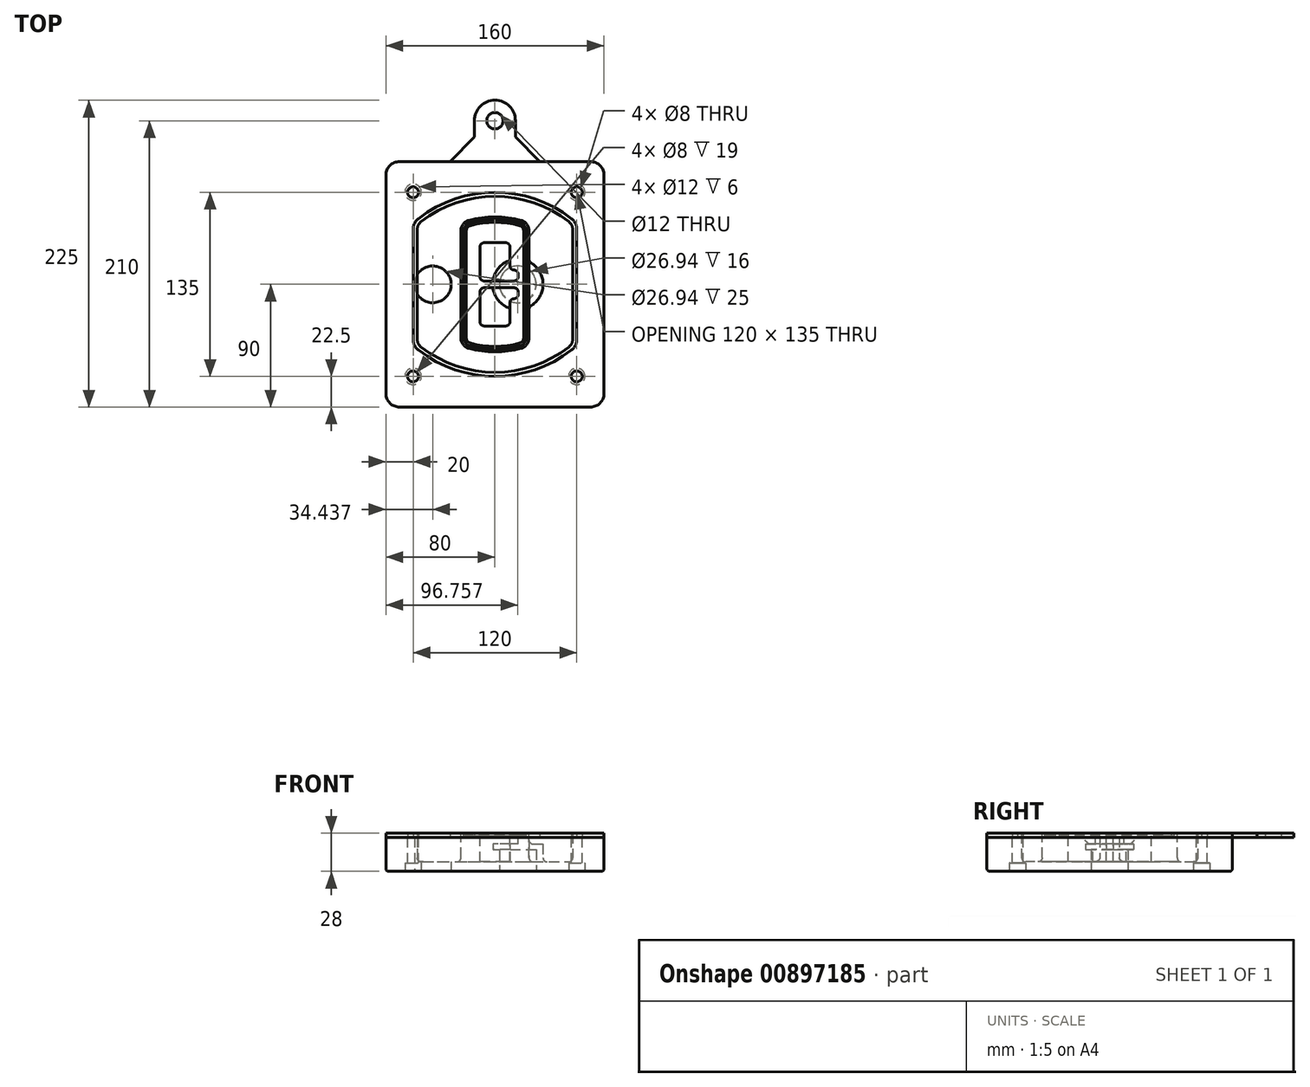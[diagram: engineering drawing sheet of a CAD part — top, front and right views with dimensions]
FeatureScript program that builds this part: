
annotation { "Feature Type Name" : "Feature", "Feature Type Description" : "" }
export const myFeature = defineFeature(function(context is Context, id is Id, definition is map)
    precondition{}
    {
        {
            var Q0;
            Q0=qCreatedBy(makeId("Top.planeOp"),FACE);
            var sketch = newSketch(context, id + "F0", { "sketchPlane" : qUnion([Q0])});
            skPoint(sketch, "E0.rect.middle", {"position": v(0, 0) * mm});
            skLineSegment(sketch, "E1.bottom", {"start": v(-70, -90) * mm, "end": v(70, -90) * mm});
            skLineSegment(sketch, "E1.top", {"start": v(-70, 90) * mm, "end": v(70, 90) * mm});
            skLineSegment(sketch, "E1.left", {"start": v(-80, -80) * mm, "end": v(-80, 80) * mm});
            skLineSegment(sketch, "E1.right", {"start": v(80, -80) * mm, "end": v(80, 80) * mm});
            skLineSegment(sketch, "E2", {"start": v(-80, 90) * mm, "end": v(80, -90) * mm, "construction": true});
            skLineSegment(sketch, "E3", {"start": v(80, 90) * mm, "end": v(-80, -90) * mm, "construction": true});
            skCircle(sketch, "E4", {"center": v(-60, 67.5) * mm, "radius": 4 * mm});
            skCircle(sketch, "E5", {"center": v(60, 67.5) * mm, "radius": 4 * mm});
            skCircle(sketch, "E6", {"center": v(60, -67.5) * mm, "radius": 4 * mm});
            skCircle(sketch, "E7", {"center": v(-60, -67.5) * mm, "radius": 4 * mm});
            skLineSegment(sketch, "E8", {"start": v(-60, 67.5) * mm, "end": v(60, 67.5) * mm, "construction": true});
            skLineSegment(sketch, "E9", {"start": v(60, 67.5) * mm, "end": v(60, -67.5) * mm, "construction": true});
            skLineSegment(sketch, "E10", {"start": v(60, -67.5) * mm, "end": v(-60, -67.5) * mm, "construction": true});
            skLineSegment(sketch, "E11", {"start": v(-60, -67.5) * mm, "end": v(-60, 67.5) * mm, "construction": true});
            skLineSegment(sketch, "E12", {"start": v(-60, 40.3) * mm, "end": v(-60, -40.3) * mm});
            skLineSegment(sketch, "E13", {"start": v(60, 40.3) * mm, "end": v(60, -40.3) * mm});
            skArc(sketch, "E14", {"start": v(56.15, 48.18) * mm, "mid": v(0, 67.5) * mm, "end": v(-56.15, 48.18) * mm});
            skArc(sketch, "E15", {"start": v(-56.15, -48.18) * mm, "mid": v(0, -67.5) * mm, "end": v(56.15, -48.18) * mm});
            skLineSegment(sketch, "E16", {"start": v(-60, 0) * mm, "end": v(60, 0) * mm, "construction": true});
            skPoint(sketch, "E17.visualSharp", {"position": v(-60, -45) * mm});
            skArc(sketch, "E17.filletArc", {"start": v(-60, -40.3) * mm, "mid": v(-58.99, -44.68) * mm, "end": v(-56.15, -48.18) * mm});
            skPoint(sketch, "E18.visualSharp", {"position": v(-60, 45) * mm});
            skArc(sketch, "E18.filletArc", {"start": v(-56.15, 48.18) * mm, "mid": v(-58.99, 44.68) * mm, "end": v(-60, 40.3) * mm});
            skPoint(sketch, "E19.visualSharp", {"position": v(60, 45) * mm});
            skArc(sketch, "E19.filletArc", {"start": v(60, 40.3) * mm, "mid": v(58.99, 44.68) * mm, "end": v(56.15, 48.18) * mm});
            skPoint(sketch, "E20.visualSharp", {"position": v(60, -45) * mm});
            skArc(sketch, "E20.filletArc", {"start": v(56.15, -48.18) * mm, "mid": v(58.99, -44.68) * mm, "end": v(60, -40.3) * mm});
            skPoint(sketch, "E21.visualSharp", {"position": v(-80, 90) * mm});
            skArc(sketch, "E21.filletArc", {"start": v(-70, 90) * mm, "mid": v(-77.07, 87.07) * mm, "end": v(-80, 80) * mm});
            skPoint(sketch, "E22.visualSharp", {"position": v(80, 90) * mm});
            skArc(sketch, "E22.filletArc", {"start": v(80, 80) * mm, "mid": v(77.07, 87.07) * mm, "end": v(70, 90) * mm});
            skPoint(sketch, "E23.visualSharp", {"position": v(80, -90) * mm});
            skArc(sketch, "E23.filletArc", {"start": v(70, -90) * mm, "mid": v(77.07, -87.07) * mm, "end": v(80, -80) * mm});
            skPoint(sketch, "E24.visualSharp", {"position": v(-80, -90) * mm});
            skArc(sketch, "E24.filletArc", {"start": v(-80, -80) * mm, "mid": v(-77.07, -87.07) * mm, "end": v(-70, -90) * mm});
            skArc(sketch, "E25.0", {"start": v(57, 40.3) * mm, "mid": v(56.3, 43.36) * mm, "end": v(54.3, 45.81) * mm});
            skLineSegment(sketch, "E25.1", {"start": v(57, 40.3) * mm, "end": v(57, -40.3) * mm});
            skArc(sketch, "E25.2", {"start": v(54.3, -45.81) * mm, "mid": v(56.3, -43.36) * mm, "end": v(57, -40.3) * mm});
            skArc(sketch, "E25.3", {"start": v(-54.3, -45.81) * mm, "mid": v(0, -64.5) * mm, "end": v(54.3, -45.81) * mm});
            skArc(sketch, "E25.4", {"start": v(-57, -40.3) * mm, "mid": v(-56.3, -43.36) * mm, "end": v(-54.3, -45.81) * mm});
            skArc(sketch, "E25.5", {"start": v(54.3, 45.81) * mm, "mid": v(0, 64.5) * mm, "end": v(-54.3, 45.81) * mm});
            skLineSegment(sketch, "E25.6", {"start": v(-57, 40.3) * mm, "end": v(-57, -40.3) * mm});
            skArc(sketch, "E25.7", {"start": v(-54.3, 45.81) * mm, "mid": v(-56.3, 43.36) * mm, "end": v(-57, 40.3) * mm});
            skArc(sketch, "E26.0", {"start": v(-58.62, 51.33) * mm, "mid": v(-62.58, 46.43) * mm, "end": v(-64, 40.3) * mm});
            skArc(sketch, "E26.1", {"start": v(58.62, 51.33) * mm, "mid": v(0, 71.5) * mm, "end": v(-58.62, 51.33) * mm});
            skArc(sketch, "E26.2", {"start": v(64, 40.3) * mm, "mid": v(62.58, 46.43) * mm, "end": v(58.62, 51.33) * mm});
            skLineSegment(sketch, "E26.3", {"start": v(64, 40.3) * mm, "end": v(64, -40.3) * mm});
            skArc(sketch, "E26.4", {"start": v(58.62, -51.33) * mm, "mid": v(62.58, -46.43) * mm, "end": v(64, -40.3) * mm});
            skLineSegment(sketch, "E26.5", {"start": v(-64, 40.3) * mm, "end": v(-64, -40.3) * mm});
            skArc(sketch, "E26.6", {"start": v(-58.62, -51.33) * mm, "mid": v(0, -71.5) * mm, "end": v(58.62, -51.33) * mm});
            skArc(sketch, "E26.7", {"start": v(-64, -40.3) * mm, "mid": v(-62.58, -46.43) * mm, "end": v(-58.62, -51.33) * mm});
            skSolve(sketch);
        }
        {
            var Q0;
            Q0=makeQuery(id+"F0.imprint","IMPRINT",FACE,{"disambiguationData":[TD([[makeQuery(id+"F0.imprint","IMPRINT",EDGE,{"derivedFrom":sQuery(id+"F0.wireOp",EDGE,"E1.bottom")}),1.0]])]});
            var Q1;
            Q1=makeQuery(id+"F0.imprint","IMPRINT",FACE,{"disambiguationData":[TD([[makeQuery(id+"F0.imprint","IMPRINT",EDGE,{"derivedFrom":sQuery(id+"F0.wireOp",EDGE,"E12")}),1.0]])]});
            var Q2;
            Q2=makeQuery(id+"F0.imprint","IMPRINT",FACE,{"disambiguationData":[TD([[makeQuery(id+"F0.imprint","IMPRINT",EDGE,{"derivedFrom":sQuery(id+"F0.wireOp",EDGE,"E25.0")}),1.0]])]});
            var Q3;
            Q3=makeQuery(id+"F0.imprint","IMPRINT",FACE,{"disambiguationData":[TD([[makeQuery(id+"F0.imprint","IMPRINT",EDGE,{"derivedFrom":sQuery(id+"F0.wireOp",EDGE,"E12")}),-1.0]])]});
            extrude(context, id + "F1", {"entities" : qUnion([Q0, Q1, Q2, Q3]), "oppositeDirection" : true, "depth" : 25 * mm});
        }
        {
            var Q0;
            Q0=makeQuery(id+"F0.imprint","IMPRINT",FACE,{"disambiguationData":[TD([[makeQuery(id+"F0.imprint","IMPRINT",EDGE,{"derivedFrom":sQuery(id+"F0.wireOp",EDGE,"E12")}),1.0]])]});
            extrude(context, id + "F2", {"entities" : qUnion([Q0]), "operationType" : NewBodyOperationType.ADD, "depth" : 3 * mm});
        }
        {
            var Q0;
            Q0=makeQuery(id+"F0.imprint","IMPRINT",FACE,{"disambiguationData":[TD([[makeQuery(id+"F0.imprint","IMPRINT",EDGE,{"derivedFrom":sQuery(id+"F0.wireOp",EDGE,"E25.0")}),1.0]])]});
            extrude(context, id + "F3", {"entities" : qUnion([Q0]), "operationType" : NewBodyOperationType.REMOVE, "oppositeDirection" : true, "depth" : 18 * mm});
        }
        {
            var Q0;
            Q0=makeQuery(id+"F2.opExtrude","CAP_FACE",FACE,{"disambiguationData":[OSD([sQuery(id+"F0.wireOp",EDGE,"E12"),sQuery(id+"F0.wireOp",EDGE,"E13"),sQuery(id+"F0.wireOp",EDGE,"E14"),sQuery(id+"F0.wireOp",EDGE,"E15"),sQuery(id+"F0.wireOp",EDGE,"E17.filletArc"),sQuery(id+"F0.wireOp",EDGE,"E18.filletArc"),sQuery(id+"F0.wireOp",EDGE,"E19.filletArc"),sQuery(id+"F0.wireOp",EDGE,"E20.filletArc"),sQuery(id+"F0.wireOp",EDGE,"E25.0"),sQuery(id+"F0.wireOp",EDGE,"E25.1"),sQuery(id+"F0.wireOp",EDGE,"E25.2"),sQuery(id+"F0.wireOp",EDGE,"E25.3"),sQuery(id+"F0.wireOp",EDGE,"E25.4"),sQuery(id+"F0.wireOp",EDGE,"E25.5"),sQuery(id+"F0.wireOp",EDGE,"E25.6"),sQuery(id+"F0.wireOp",EDGE,"E25.7")])],"isStart":false});
            var sketch = newSketch(context, id + "F4", { "sketchPlane" : qUnion([Q0])});
            skArc(sketch, "E27.0", {"start": v(-19.08, -46.97) * mm, "mid": v(0, -49.5) * mm, "end": v(19.08, -46.97) * mm});
            skArc(sketch, "E28.0", {"start": v(19.08, 46.97) * mm, "mid": v(0, 49.5) * mm, "end": v(-19.08, 46.97) * mm});
            skLineSegment(sketch, "E29", {"start": v(-25, 39.25) * mm, "end": v(-25, -39.25) * mm});
            skLineSegment(sketch, "E30", {"start": v(25, 39.25) * mm, "end": v(25, -39.25) * mm});
            skLineSegment(sketch, "E31", {"start": v(-25, 45.1) * mm, "end": v(25, 45.1) * mm, "construction": true});
            skLineSegment(sketch, "E32", {"start": v(-25, -45.1) * mm, "end": v(25, -45.1) * mm, "construction": true});
            skPoint(sketch, "E33.visualSharp", {"position": v(-25, 45.1) * mm});
            skArc(sketch, "E33.filletArc", {"start": v(-19.08, 46.97) * mm, "mid": v(-23.35, 44.11) * mm, "end": v(-25, 39.25) * mm});
            skPoint(sketch, "E34.visualSharp", {"position": v(25, 45.1) * mm});
            skArc(sketch, "E34.filletArc", {"start": v(25, 39.25) * mm, "mid": v(23.35, 44.11) * mm, "end": v(19.08, 46.97) * mm});
            skPoint(sketch, "E35.visualSharp", {"position": v(25, -45.1) * mm});
            skArc(sketch, "E35.filletArc", {"start": v(19.08, -46.97) * mm, "mid": v(23.35, -44.11) * mm, "end": v(25, -39.25) * mm});
            skPoint(sketch, "E36.visualSharp", {"position": v(-25, -45.1) * mm});
            skArc(sketch, "E36.filletArc", {"start": v(-25, -39.25) * mm, "mid": v(-23.35, -44.11) * mm, "end": v(-19.08, -46.97) * mm});
            skArc(sketch, "E37.0", {"start": v(54.3, 45.81) * mm, "mid": v(0, 64.5) * mm, "end": v(-54.3, 45.81) * mm});
            skArc(sketch, "E37.1", {"start": v(-54.3, 45.81) * mm, "mid": v(-56.3, 43.36) * mm, "end": v(-57, 40.3) * mm});
            skLineSegment(sketch, "E37.2", {"start": v(-57, 40.3) * mm, "end": v(-57, -40.3) * mm});
            skArc(sketch, "E37.3", {"start": v(-57, -40.3) * mm, "mid": v(-56.3, -43.36) * mm, "end": v(-54.3, -45.81) * mm});
            skArc(sketch, "E37.4", {"start": v(-54.3, -45.81) * mm, "mid": v(0, -64.5) * mm, "end": v(54.3, -45.81) * mm});
            skArc(sketch, "E37.5", {"start": v(54.3, -45.81) * mm, "mid": v(56.3, -43.36) * mm, "end": v(57, -40.3) * mm});
            skLineSegment(sketch, "E37.6", {"start": v(57, 40.3) * mm, "end": v(57, -40.3) * mm});
            skArc(sketch, "E37.7", {"start": v(57, 40.3) * mm, "mid": v(56.3, 43.36) * mm, "end": v(54.3, 45.81) * mm});
            skLineSegment(sketch, "E38.0", {"start": v(23, 39.25) * mm, "end": v(23, -39.25) * mm});
            skArc(sketch, "E38.1", {"start": v(18.56, -45.04) * mm, "mid": v(21.76, -42.9) * mm, "end": v(23, -39.25) * mm});
            skArc(sketch, "E38.2", {"start": v(-18.56, -45.04) * mm, "mid": v(0, -47.5) * mm, "end": v(18.56, -45.04) * mm});
            skArc(sketch, "E38.3", {"start": v(-23, -39.25) * mm, "mid": v(-21.76, -42.9) * mm, "end": v(-18.56, -45.04) * mm});
            skLineSegment(sketch, "E38.4", {"start": v(-23, 39.25) * mm, "end": v(-23, -39.25) * mm});
            skArc(sketch, "E38.5", {"start": v(23, 39.25) * mm, "mid": v(21.76, 42.9) * mm, "end": v(18.56, 45.04) * mm});
            skArc(sketch, "E38.6", {"start": v(-18.56, 45.04) * mm, "mid": v(-21.76, 42.9) * mm, "end": v(-23, 39.25) * mm});
            skArc(sketch, "E38.7", {"start": v(18.56, 45.04) * mm, "mid": v(0, 47.5) * mm, "end": v(-18.56, 45.04) * mm});
            skArc(sketch, "E39.0", {"start": v(21, 39.25) * mm, "mid": v(20.18, 41.68) * mm, "end": v(18.04, 43.1) * mm});
            skLineSegment(sketch, "E39.1", {"start": v(21, 39.25) * mm, "end": v(21, -39.25) * mm});
            skArc(sketch, "E39.2", {"start": v(18.04, -43.1) * mm, "mid": v(20.18, -41.68) * mm, "end": v(21, -39.25) * mm});
            skArc(sketch, "E39.3", {"start": v(-18.04, -43.1) * mm, "mid": v(0, -45.5) * mm, "end": v(18.04, -43.1) * mm});
            skArc(sketch, "E39.4", {"start": v(-21, -39.25) * mm, "mid": v(-20.18, -41.68) * mm, "end": v(-18.04, -43.1) * mm});
            skArc(sketch, "E39.5", {"start": v(18.04, 43.1) * mm, "mid": v(0, 45.5) * mm, "end": v(-18.04, 43.1) * mm});
            skLineSegment(sketch, "E39.6", {"start": v(-21, 39.25) * mm, "end": v(-21, -39.25) * mm});
            skArc(sketch, "E39.7", {"start": v(-18.04, 43.1) * mm, "mid": v(-20.18, 41.68) * mm, "end": v(-21, 39.25) * mm});
            skLineSegment(sketch, "E40", {"start": v(-25, 0) * mm, "end": v(25, 0) * mm, "construction": true});
            skLineSegment(sketch, "E41", {"start": v(-11, 5.5) * mm, "end": v(-11, 27.5) * mm});
            skLineSegment(sketch, "E42", {"start": v(-8, 30.5) * mm, "end": v(8, 30.5) * mm});
            skLineSegment(sketch, "E43", {"start": v(11, 27.5) * mm, "end": v(11, 13.5) * mm});
            skLineSegment(sketch, "E44", {"start": v(14, 10.5) * mm, "end": v(14, 10.5) * mm});
            skLineSegment(sketch, "E45", {"start": v(17, 7.5) * mm, "end": v(17, 5.5) * mm});
            skLineSegment(sketch, "E46", {"start": v(14, 2.5) * mm, "end": v(-8, 2.5) * mm});
            skPoint(sketch, "E47.visualSharp", {"position": v(-11, 30.5) * mm});
            skArc(sketch, "E47.filletArc", {"start": v(-8, 30.5) * mm, "mid": v(-10.12, 29.62) * mm, "end": v(-11, 27.5) * mm});
            skPoint(sketch, "E48.visualSharp", {"position": v(11, 30.5) * mm});
            skArc(sketch, "E48.filletArc", {"start": v(11, 27.5) * mm, "mid": v(10.12, 29.62) * mm, "end": v(8, 30.5) * mm});
            skPoint(sketch, "E49.visualSharp", {"position": v(11, 10.5) * mm});
            skArc(sketch, "E49.filletArc", {"start": v(11, 13.5) * mm, "mid": v(11.88, 11.38) * mm, "end": v(14, 10.5) * mm});
            skPoint(sketch, "E50.visualSharp", {"position": v(17, 10.5) * mm});
            skArc(sketch, "E50.filletArc", {"start": v(17, 7.5) * mm, "mid": v(16.12, 9.62) * mm, "end": v(14, 10.5) * mm});
            skPoint(sketch, "E51.visualSharp", {"position": v(17, 2.5) * mm});
            skArc(sketch, "E51.filletArc", {"start": v(14, 2.5) * mm, "mid": v(16.12, 3.38) * mm, "end": v(17, 5.5) * mm});
            skPoint(sketch, "E52.visualSharp", {"position": v(-11, 2.5) * mm});
            skArc(sketch, "E52.filletArc", {"start": v(-11, 5.5) * mm, "mid": v(-10.12, 3.38) * mm, "end": v(-8, 2.5) * mm});
            skLineSegment(sketch, "E53.0.MirrorCS", {"start": v(14, -2.5) * mm, "end": v(-8, -2.5) * mm});
            skArc(sketch, "E54.0.MirrorCS", {"start": v(-11, -5.5) * mm, "mid": v(-10.12, -3.38) * mm, "end": v(-8, -2.5) * mm});
            skLineSegment(sketch, "E55.0.MirrorCS", {"start": v(-11, -5.5) * mm, "end": v(-11, -27.5) * mm});
            skArc(sketch, "E56.0.MirrorCS", {"start": v(-8, -30.5) * mm, "mid": v(-10.12, -29.62) * mm, "end": v(-11, -27.5) * mm});
            skLineSegment(sketch, "E57.0.MirrorCS", {"start": v(-8, -30.5) * mm, "end": v(8, -30.5) * mm});
            skArc(sketch, "E58.0.MirrorCS", {"start": v(11, -27.5) * mm, "mid": v(10.12, -29.62) * mm, "end": v(8, -30.5) * mm});
            skLineSegment(sketch, "E59.0.MirrorCS", {"start": v(11, -27.5) * mm, "end": v(11, -13.5) * mm});
            skArc(sketch, "E60.0.MirrorCS", {"start": v(11, -13.5) * mm, "mid": v(11.88, -11.38) * mm, "end": v(14, -10.5) * mm});
            skArc(sketch, "E61.0.MirrorCS", {"start": v(17, -7.5) * mm, "mid": v(16.12, -9.62) * mm, "end": v(14, -10.5) * mm});
            skLineSegment(sketch, "E62.0.MirrorCS", {"start": v(17, -7.5) * mm, "end": v(17, -5.5) * mm});
            skArc(sketch, "E63.0.MirrorCS", {"start": v(14, -2.5) * mm, "mid": v(16.12, -3.38) * mm, "end": v(17, -5.5) * mm});
            skSolve(sketch);
        }
        {
            var Q0;
            Q0=makeQuery(id+"F4.imprint","IMPRINT",FACE,{"disambiguationData":[TD([[makeQuery(id+"F4.imprint","IMPRINT",EDGE,{"derivedFrom":sQuery(id+"F4.wireOp",EDGE,"E27.0")}),1.0]])]});
            var Q1;
            Q1=makeQuery(id+"F4.imprint","IMPRINT",FACE,{"disambiguationData":[TD([[makeQuery(id+"F4.imprint","IMPRINT",EDGE,{"derivedFrom":sQuery(id+"F4.wireOp",EDGE,"E38.0")}),-1.0]])]});
            var Q2;
            Q2=makeQuery(id+"F4.imprint","IMPRINT",FACE,{"disambiguationData":[TD([[makeQuery(id+"F4.imprint","IMPRINT",EDGE,{"derivedFrom":sQuery(id+"F4.wireOp",EDGE,"E39.0")}),1.0]])]});
            extrude(context, id + "F5", {"entities" : qUnion([Q0, Q1, Q2]), "operationType" : NewBodyOperationType.ADD, "endBound" : BoundingType.UP_TO_NEXT, "oppositeDirection" : true, "depth" : 25 * mm});
        }
        {
            var Q0;
            Q0=makeQuery(id+"F4.imprint","IMPRINT",FACE,{"disambiguationData":[TD([[makeQuery(id+"F4.imprint","IMPRINT",EDGE,{"derivedFrom":sQuery(id+"F4.wireOp",EDGE,"E38.0")}),-1.0]])]});
            extrude(context, id + "F6", {"entities" : qUnion([Q0]), "operationType" : NewBodyOperationType.REMOVE, "oppositeDirection" : true, "depth" : 2 * mm});
        }
        {
            var Q0;
            Q0=makeQuery(id+"F1.opExtrude","CAP_FACE",FACE,{"disambiguationData":[OSD([sQuery(id+"F0.wireOp",EDGE,"E1.bottom"),sQuery(id+"F0.wireOp",EDGE,"E1.top"),sQuery(id+"F0.wireOp",EDGE,"E1.left"),sQuery(id+"F0.wireOp",EDGE,"E1.right"),sQuery(id+"F0.wireOp",EDGE,"E4"),sQuery(id+"F0.wireOp",EDGE,"E5"),sQuery(id+"F0.wireOp",EDGE,"E6"),sQuery(id+"F0.wireOp",EDGE,"E7"),sQuery(id+"F0.wireOp",EDGE,"E21.filletArc"),sQuery(id+"F0.wireOp",EDGE,"E22.filletArc"),sQuery(id+"F0.wireOp",EDGE,"E23.filletArc"),sQuery(id+"F0.wireOp",EDGE,"E24.filletArc")])],"isStart":false});
            var sketch = newSketch(context, id + "F7", { "sketchPlane" : qUnion([Q0])});
            skCircle(sketch, "E64", {"center": v(16.76, 0) * mm, "radius": 13.47 * mm});
            skCircle(sketch, "E65", {"center": v(-45.56, 0) * mm, "radius": 13.47 * mm});
            skLineSegment(sketch, "E66", {"start": v(80, 0) * mm, "end": v(-80, 0) * mm});
            skCircle(sketch, "E67", {"center": v(16.76, 0) * mm, "radius": 18.47 * mm});
            skCircle(sketch, "E68", {"center": v(60, -67.5) * mm, "radius": 6 * mm});
            skCircle(sketch, "E69", {"center": v(-60, -67.5) * mm, "radius": 6 * mm});
            skCircle(sketch, "E70", {"center": v(-60, 67.5) * mm, "radius": 6 * mm});
            skCircle(sketch, "E71", {"center": v(60, 67.5) * mm, "radius": 6 * mm});
            skSolve(sketch);
        }
        {
            var Q0;
            {var subQ1=sQuery(id+"F7.wireOp",EDGE,"E66");var subQ4=sQuery(id+"F7.wireOp",EDGE,"E64");var subQ6=makeQuery(id+"F7.imprint","INTERSECT",VERTEX,{"disambiguationData":[OD(0.0)],"derivedFrom":[subQ4,subQ1]});Q0=makeQuery(id+"F7.imprint","IMPRINT",FACE,{"disambiguationData":[TD([[makeQuery(id+"F7.imprint","IMPRINT",EDGE,{"disambiguationData":[TD([[subQ6,-1.0]])],"derivedFrom":subQ4}),-1.0]])]});}
            var Q1;
            {var subQ0=sQuery(id+"F7.wireOp",EDGE,"E66");var subQ1=sQuery(id+"F7.wireOp",EDGE,"E64");var subQ3=makeQuery(id+"F7.imprint","INTERSECT",VERTEX,{"disambiguationData":[OD(0.0)],"derivedFrom":[subQ1,subQ0]});Q1=makeQuery(id+"F7.imprint","IMPRINT",FACE,{"disambiguationData":[TD([[makeQuery(id+"F7.imprint","IMPRINT",EDGE,{"disambiguationData":[TD([[subQ3,-1.0]])],"derivedFrom":subQ1}),1.0]])]});}
            var Q2;
            {var subQ0=sQuery(id+"F7.wireOp",EDGE,"E66");var subQ1=sQuery(id+"F7.wireOp",EDGE,"E64");var subQ3=makeQuery(id+"F7.imprint","INTERSECT",VERTEX,{"disambiguationData":[OD(0.0)],"derivedFrom":[subQ1,subQ0]});Q2=makeQuery(id+"F7.imprint","IMPRINT",FACE,{"disambiguationData":[TD([[makeQuery(id+"F7.imprint","IMPRINT",EDGE,{"disambiguationData":[TD([[subQ3,1.0]])],"derivedFrom":subQ1}),1.0]])]});}
            var Q3;
            {var subQ1=sQuery(id+"F7.wireOp",EDGE,"E66");var subQ4=sQuery(id+"F7.wireOp",EDGE,"E64");var subQ6=makeQuery(id+"F7.imprint","INTERSECT",VERTEX,{"disambiguationData":[OD(0.0)],"derivedFrom":[subQ4,subQ1]});Q3=makeQuery(id+"F7.imprint","IMPRINT",FACE,{"disambiguationData":[TD([[makeQuery(id+"F7.imprint","IMPRINT",EDGE,{"disambiguationData":[TD([[subQ6,1.0]])],"derivedFrom":subQ4}),-1.0]])]});}
            extrude(context, id + "F8", {"entities" : qUnion([Q0, Q1, Q2, Q3]), "operationType" : NewBodyOperationType.ADD, "oppositeDirection" : true, "depth" : 20 * mm});
        }
        {
            var Q0;
            {var subQ0=sQuery(id+"F7.wireOp",EDGE,"E66");var subQ1=sQuery(id+"F7.wireOp",EDGE,"E64");var subQ3=makeQuery(id+"F7.imprint","INTERSECT",VERTEX,{"disambiguationData":[OD(0.0)],"derivedFrom":[subQ1,subQ0]});Q0=makeQuery(id+"F7.imprint","IMPRINT",FACE,{"disambiguationData":[TD([[makeQuery(id+"F7.imprint","IMPRINT",EDGE,{"disambiguationData":[TD([[subQ3,-1.0]])],"derivedFrom":subQ1}),1.0]])]});}
            var Q1;
            {var subQ0=sQuery(id+"F7.wireOp",EDGE,"E66");var subQ1=sQuery(id+"F7.wireOp",EDGE,"E64");var subQ3=makeQuery(id+"F7.imprint","INTERSECT",VERTEX,{"disambiguationData":[OD(0.0)],"derivedFrom":[subQ1,subQ0]});Q1=makeQuery(id+"F7.imprint","IMPRINT",FACE,{"disambiguationData":[TD([[makeQuery(id+"F7.imprint","IMPRINT",EDGE,{"disambiguationData":[TD([[subQ3,1.0]])],"derivedFrom":subQ1}),1.0]])]});}
            extrude(context, id + "F9", {"entities" : qUnion([Q0, Q1]), "operationType" : NewBodyOperationType.REMOVE, "oppositeDirection" : true, "depth" : 16 * mm});
        }
        {
            var Q0;
            {var subQ0=sQuery(id+"F7.wireOp",EDGE,"E66");var subQ1=sQuery(id+"F7.wireOp",EDGE,"E65");var subQ3=makeQuery(id+"F7.imprint","INTERSECT",VERTEX,{"disambiguationData":[OD(0.0)],"derivedFrom":[subQ1,subQ0]});Q0=makeQuery(id+"F7.imprint","IMPRINT",FACE,{"disambiguationData":[TD([[makeQuery(id+"F7.imprint","IMPRINT",EDGE,{"disambiguationData":[TD([[subQ3,-1.0]])],"derivedFrom":subQ1}),1.0]])]});}
            var Q1;
            {var subQ0=sQuery(id+"F7.wireOp",EDGE,"E66");var subQ1=sQuery(id+"F7.wireOp",EDGE,"E65");var subQ3=makeQuery(id+"F7.imprint","INTERSECT",VERTEX,{"disambiguationData":[OD(0.0)],"derivedFrom":[subQ1,subQ0]});Q1=makeQuery(id+"F7.imprint","IMPRINT",FACE,{"disambiguationData":[TD([[makeQuery(id+"F7.imprint","IMPRINT",EDGE,{"disambiguationData":[TD([[subQ3,1.0]])],"derivedFrom":subQ1}),1.0]])]});}
            extrude(context, id + "F10", {"entities" : qUnion([Q0, Q1]), "operationType" : NewBodyOperationType.REMOVE, "oppositeDirection" : true, "depth" : 25 * mm});
        }
        {
            var Q0;
            Q0=makeQuery(id+"F7.imprint","IMPRINT",FACE,{"disambiguationData":[TD([[makeQuery(id+"F7.imprint","IMPRINT",EDGE,{"derivedFrom":sQuery(id+"F7.wireOp",EDGE,"E68")}),1.0]])]});
            var Q1;
            Q1=makeQuery(id+"F7.imprint","IMPRINT",FACE,{"disambiguationData":[TD([[makeQuery(id+"F7.imprint","IMPRINT",EDGE,{"derivedFrom":makeQuery(id+"F1.opExtrude","CAP_EDGE",EDGE,{"disambiguationData":[OSD([sQuery(id+"F0.wireOp",EDGE,"E5")])],"isStart":false})}),-1.0]])]});
            var Q2;
            Q2=makeQuery(id+"F7.imprint","IMPRINT",FACE,{"disambiguationData":[TD([[makeQuery(id+"F7.imprint","IMPRINT",EDGE,{"derivedFrom":sQuery(id+"F7.wireOp",EDGE,"E69")}),1.0]])]});
            var Q3;
            Q3=makeQuery(id+"F7.imprint","IMPRINT",FACE,{"disambiguationData":[TD([[makeQuery(id+"F7.imprint","IMPRINT",EDGE,{"derivedFrom":makeQuery(id+"F1.opExtrude","CAP_EDGE",EDGE,{"disambiguationData":[OSD([sQuery(id+"F0.wireOp",EDGE,"E4")])],"isStart":false})}),-1.0]])]});
            var Q4;
            Q4=makeQuery(id+"F7.imprint","IMPRINT",FACE,{"disambiguationData":[TD([[makeQuery(id+"F7.imprint","IMPRINT",EDGE,{"derivedFrom":sQuery(id+"F7.wireOp",EDGE,"E70")}),1.0]])]});
            var Q5;
            Q5=makeQuery(id+"F7.imprint","IMPRINT",FACE,{"disambiguationData":[TD([[makeQuery(id+"F7.imprint","IMPRINT",EDGE,{"derivedFrom":makeQuery(id+"F1.opExtrude","CAP_EDGE",EDGE,{"disambiguationData":[OSD([sQuery(id+"F0.wireOp",EDGE,"E7")])],"isStart":false})}),-1.0]])]});
            var Q6;
            Q6=makeQuery(id+"F7.imprint","IMPRINT",FACE,{"disambiguationData":[TD([[makeQuery(id+"F7.imprint","IMPRINT",EDGE,{"derivedFrom":sQuery(id+"F7.wireOp",EDGE,"E71")}),1.0]])]});
            var Q7;
            Q7=makeQuery(id+"F7.imprint","IMPRINT",FACE,{"disambiguationData":[TD([[makeQuery(id+"F7.imprint","IMPRINT",EDGE,{"derivedFrom":makeQuery(id+"F1.opExtrude","CAP_EDGE",EDGE,{"disambiguationData":[OSD([sQuery(id+"F0.wireOp",EDGE,"E6")])],"isStart":false})}),-1.0]])]});
            extrude(context, id + "F11", {"entities" : qUnion([Q0, Q1, Q2, Q3, Q4, Q5, Q6, Q7]), "operationType" : NewBodyOperationType.REMOVE, "oppositeDirection" : true, "depth" : 6 * mm});
        }
        {
            var Q0;
            Q0=makeQuery(id+"F9.boolean.opBoolean","COPY",FACE,{"derivedFrom":makeQuery(id+"F9.opExtrude","CAP_FACE",FACE,{"disambiguationData":[OSD([sQuery(id+"F7.wireOp",EDGE,"E64")])],"isStart":false})});
            var sketch = newSketch(context, id + "F12", { "sketchPlane" : qUnion([Q0])});
            skArc(sketch, "E72.0", {"start": v(11, 17.55) * mm, "mid": v(2.57, 11.82) * mm, "end": v(-1.54, 2.5) * mm});
            skArc(sketch, "E72.1", {"start": v(-1.54, -2.5) * mm, "mid": v(2.57, -11.82) * mm, "end": v(11, -17.55) * mm});
            skLineSegment(sketch, "E73", {"start": v(-1.54, -2.5) * mm, "end": v(14, -2.5) * mm});
            skLineSegment(sketch, "E74.0", {"start": v(14, 2.5) * mm, "end": v(-1.54, 2.5) * mm});
            skArc(sketch, "E74.1", {"start": v(14, 2.5) * mm, "mid": v(16.12, 3.38) * mm, "end": v(17, 5.5) * mm});
            skLineSegment(sketch, "E74.2", {"start": v(17, 7.5) * mm, "end": v(17, 5.5) * mm});
            skArc(sketch, "E74.3", {"start": v(17, 7.5) * mm, "mid": v(16.12, 9.62) * mm, "end": v(14, 10.5) * mm});
            skArc(sketch, "E74.4", {"start": v(11, 13.5) * mm, "mid": v(11.88, 11.38) * mm, "end": v(14, 10.5) * mm});
            skLineSegment(sketch, "E74.5", {"start": v(11, 17.55) * mm, "end": v(11, 13.5) * mm});
            skLineSegment(sketch, "E74.7", {"start": v(14, -2.5) * mm, "end": v(-1.54, -2.5) * mm});
            skArc(sketch, "E74.8", {"start": v(14, -2.5) * mm, "mid": v(16.12, -3.38) * mm, "end": v(17, -5.5) * mm});
            skLineSegment(sketch, "E74.9", {"start": v(17, -7.5) * mm, "end": v(17, -5.5) * mm});
            skArc(sketch, "E74.10", {"start": v(17, -7.5) * mm, "mid": v(16.12, -9.62) * mm, "end": v(14, -10.5) * mm});
            skArc(sketch, "E74.11", {"start": v(11, -13.5) * mm, "mid": v(11.88, -11.38) * mm, "end": v(14, -10.5) * mm});
            skLineSegment(sketch, "E74.12", {"start": v(11, -17.55) * mm, "end": v(11, -13.5) * mm});
            skPoint(sketch, "E75.orphan", {"position": v(11, -27.5) * mm});
            skPoint(sketch, "E76.orphan", {"position": v(-8, -2.5) * mm});
            skPoint(sketch, "E77.orphan", {"position": v(-8, 2.5) * mm});
            skPoint(sketch, "E78.orphan", {"position": v(11, 27.5) * mm});
            skSolve(sketch);
        }
        {
            var Q0;
            {var subQ7=sQuery(id+"F12.wireOp",EDGE,"E72.0");var subQ14=sQuery(id+"F12.wireOp",EDGE,"E72.1");var subQ16=sQuery(id+"F12.wireOp",EDGE,"E74.1");var subQ18=sQuery(id+"F12.wireOp",EDGE,"E74.8");Q0=qUnion([makeQuery(id+"F12.imprint","IMPRINT",FACE,{"disambiguationData":[TD([[makeQuery(id+"F12.imprint","IMPRINT",EDGE,{"derivedFrom":subQ7}),1.0]])]}),makeQuery(id+"F12.imprint","IMPRINT",FACE,{"disambiguationData":[TD([[makeQuery(id+"F12.imprint","IMPRINT",EDGE,{"derivedFrom":subQ14}),1.0]])]}),makeQuery(id+"F12.imprint","IMPRINT",FACE,{"disambiguationData":[TD([[makeQuery(id+"F12.imprint","IMPRINT",EDGE,{"derivedFrom":subQ16}),1.0]])]}),makeQuery(id+"F12.imprint","IMPRINT",FACE,{"disambiguationData":[TD([[makeQuery(id+"F12.imprint","IMPRINT",EDGE,{"derivedFrom":subQ18}),-1.0]])]})]);}
            var Q1;
            Q1=makeQuery(id+"F5.boolean.opBoolean","SPLIT",FACE,{"disambiguationData":[TD([makeQuery(id+"F5.opExtrude","SWEPT_FACE",FACE,{"disambiguationData":[OSD([sQuery(id+"F4.wireOp",EDGE,"E41")])]})])],"derivedFrom":makeQuery(id+"F3.boolean.opBoolean","COPY",FACE,{"derivedFrom":makeQuery(id+"F3.opExtrude","CAP_FACE",FACE,{"disambiguationData":[OSD([sQuery(id+"F0.wireOp",EDGE,"E25.0"),sQuery(id+"F0.wireOp",EDGE,"E25.1"),sQuery(id+"F0.wireOp",EDGE,"E25.2"),sQuery(id+"F0.wireOp",EDGE,"E25.3"),sQuery(id+"F0.wireOp",EDGE,"E25.4"),sQuery(id+"F0.wireOp",EDGE,"E25.5"),sQuery(id+"F0.wireOp",EDGE,"E25.6"),sQuery(id+"F0.wireOp",EDGE,"E25.7")])],"isStart":false})})});
            extrude(context, id + "F13", {"entities" : qUnion([Q0]), "operationType" : NewBodyOperationType.REMOVE, "endBound" : BoundingType.UP_TO_SURFACE, "endBoundEntityFace" : qUnion([Q1]), "depth" : 25 * mm});
        }
        {
            var Q0;
            Q0=makeQuery(id+"F3.boolean.opBoolean","COPY",EDGE,{"derivedFrom":makeQuery(id+"F3.opExtrude","CAP_EDGE",EDGE,{"disambiguationData":[OSD([sQuery(id+"F0.wireOp",EDGE,"E25.6")])],"isStart":false})});
            var Q1;
            Q1=makeQuery(id+"F8.boolean.opBoolean","INTERSECT",EDGE,{"derivedFrom":[makeQuery(id+"F5.opExtrude","SWEPT_FACE",FACE,{"disambiguationData":[OSD([sQuery(id+"F4.wireOp",EDGE,"E30")])]}),makeQuery(id+"F8.opExtrude","CAP_FACE",FACE,{"disambiguationData":[OSD([sQuery(id+"F7.wireOp",EDGE,"E67")])],"isStart":false})]});
            var Q2;
            Q2=makeQuery(id+"F8.boolean.opBoolean","INTERSECT",EDGE,{"disambiguationData":[OD(1.0)],"derivedFrom":[makeQuery(id+"F5.opExtrude","SWEPT_FACE",FACE,{"disambiguationData":[OSD([sQuery(id+"F4.wireOp",EDGE,"E30")])]}),makeQuery(id+"F8.opExtrude","SWEPT_FACE",FACE,{"disambiguationData":[OSD([sQuery(id+"F7.wireOp",EDGE,"E67")])]})]});
            var Q3;
            {var subQ0=sQuery(id+"F4.wireOp",EDGE,"E30");Q3=makeQuery(id+"F8.boolean.opBoolean","SPLIT",EDGE,{"disambiguationData":[TD([makeQuery(id+"F5.opExtrude","SWEPT_FACE",FACE,{"disambiguationData":[OSD([sQuery(id+"F4.wireOp",EDGE,"E35.filletArc")])]})])],"derivedFrom":makeQuery(id+"F5.opExtrude","CAP_EDGE",EDGE,{"disambiguationData":[OSD([subQ0])],"isStart":false})});}
            var Q4;
            {var subQ0=sQuery(id+"F0.wireOp",EDGE,"E25.7");var subQ1=sQuery(id+"F0.wireOp",EDGE,"E25.1");var subQ2=sQuery(id+"F0.wireOp",EDGE,"E25.6");var subQ3=sQuery(id+"F0.wireOp",EDGE,"E25.5");var subQ4=sQuery(id+"F0.wireOp",EDGE,"E25.4");var subQ5=sQuery(id+"F0.wireOp",EDGE,"E25.0");var subQ6=sQuery(id+"F0.wireOp",EDGE,"E25.2");var subQ7=sQuery(id+"F0.wireOp",EDGE,"E25.3");Q4=makeQuery(id+"F8.boolean.opBoolean","INTERSECT",EDGE,{"derivedFrom":[makeQuery(id+"F5.boolean.opBoolean","SPLIT",FACE,{"disambiguationData":[TD([makeQuery(id+"F2.opExtrude","SWEPT_FACE",FACE,{"disambiguationData":[OSD([subQ5])]})])],"derivedFrom":makeQuery(id+"F3.boolean.opBoolean","COPY",FACE,{"derivedFrom":makeQuery(id+"F3.opExtrude","CAP_FACE",FACE,{"disambiguationData":[OSD([subQ5,subQ1,subQ6,subQ7,subQ4,subQ3,subQ2,subQ0])],"isStart":false})})}),makeQuery(id+"F8.opExtrude","SWEPT_FACE",FACE,{"disambiguationData":[OSD([sQuery(id+"F7.wireOp",EDGE,"E67")])]})]});}
            var Q5;
            Q5=makeQuery(id+"F8.boolean.opBoolean","INTERSECT",EDGE,{"disambiguationData":[OD(0.0)],"derivedFrom":[makeQuery(id+"F5.opExtrude","SWEPT_FACE",FACE,{"disambiguationData":[OSD([sQuery(id+"F4.wireOp",EDGE,"E30")])]}),makeQuery(id+"F8.opExtrude","SWEPT_FACE",FACE,{"disambiguationData":[OSD([sQuery(id+"F7.wireOp",EDGE,"E67")])]})]});
            fillet(context, id + "F14", {"entities" : qUnion([Q0, Q1, Q2, Q3, Q4, Q5]), "radius" : 3 * mm, "tangentPropagation" : true, "allowEdgeOverflow" : false});
        }
        {
            var Q0;
            Q0=makeQuery(id+"F1.opExtrude","CAP_EDGE",EDGE,{"disambiguationData":[OSD([sQuery(id+"F0.wireOp",EDGE,"E1.bottom")])],"isStart":false});
            fillet(context, id + "F15", {"entities" : qUnion([Q0]), "radius" : 2 * mm, "tangentPropagation" : true, "allowEdgeOverflow" : false});
        }
        {
            var Q0;
            {var subQ0=sQuery(id+"F0.wireOp",EDGE,"E21.filletArc");var subQ1=sQuery(id+"F0.wireOp",EDGE,"E7");var subQ2=sQuery(id+"F0.wireOp",EDGE,"E6");var subQ3=sQuery(id+"F0.wireOp",EDGE,"E5");var subQ4=sQuery(id+"F0.wireOp",EDGE,"E4");var subQ5=sQuery(id+"F0.wireOp",EDGE,"E22.filletArc");var subQ6=sQuery(id+"F0.wireOp",EDGE,"E1.bottom");var subQ7=sQuery(id+"F0.wireOp",EDGE,"E1.right");var subQ8=sQuery(id+"F0.wireOp",EDGE,"E1.top");var subQ9=sQuery(id+"F0.wireOp",EDGE,"E1.left");var subQ10=sQuery(id+"F0.wireOp",EDGE,"E23.filletArc");var subQ11=sQuery(id+"F0.wireOp",EDGE,"E24.filletArc");Q0=makeQuery(id+"F2.boolean.opBoolean","SPLIT",FACE,{"disambiguationData":[TD([makeQuery(id+"F1.opExtrude","SWEPT_FACE",FACE,{"disambiguationData":[OSD([subQ6])]})])],"derivedFrom":makeQuery(id+"F1.opExtrude","CAP_FACE",FACE,{"disambiguationData":[OSD([subQ6,subQ8,subQ9,subQ7,subQ4,subQ3,subQ2,subQ1,subQ0,subQ5,subQ10,subQ11])],"isStart":true})});}
            var sketch = newSketch(context, id + "F16", { "sketchPlane" : qUnion([Q0])});
            skSolve(sketch);
        }
        {
            var Q0;
            Q0=makeQuery(id+"F16.imprint","IMPRINT",FACE,{"disambiguationData":[TD([[makeQuery(id+"F16.imprint","IMPRINT",EDGE,{"derivedFrom":makeQuery(id+"F1.opExtrude","CAP_EDGE",EDGE,{"disambiguationData":[OSD([sQuery(id+"F0.wireOp",EDGE,"E1.bottom")])],"isStart":true})}),1.0]])]});
            var sketch = newSketch(context, id + "F17", { "sketchPlane" : qUnion([Q0])});
            skLineSegment(sketch, "E79", {"start": v(-33, 90) * mm, "end": v(-15, 108) * mm});
            skLineSegment(sketch, "E80", {"start": v(-15, 108) * mm, "end": v(-15, 120) * mm});
            skArc(sketch, "E81", {"start": v(15, 120) * mm, "mid": v(0, 135) * mm, "end": v(-15, 120) * mm});
            skCircle(sketch, "E82", {"center": v(0, 120) * mm, "radius": 6 * mm});
            skLineSegment(sketch, "E83", {"start": v(15, 120) * mm, "end": v(15, 108) * mm});
            skLineSegment(sketch, "E84", {"start": v(15, 108) * mm, "end": v(33, 90) * mm});
            skLineSegment(sketch, "E85", {"start": v(0, 120) * mm, "end": v(0, 95.69) * mm, "construction": true});
            skPoint(sketch, "E86.orphan", {"position": v(0, 105) * mm});
            skLineSegment(sketch, "E87.0", {"start": v(-70, 90) * mm, "end": v(70, 90) * mm, "construction": true});
            skLineSegment(sketch, "E88", {"start": v(-74.48, 0) * mm, "end": v(75.8, 0) * mm, "construction": true});
            skArc(sketch, "E89.MirrorCS", {"start": v(15, -120) * mm, "mid": v(0, -135) * mm, "end": v(-15, -120) * mm});
            skPoint(sketch, "E90.MirrorP", {"position": v(0, -105) * mm});
            skLineSegment(sketch, "E91.MirrorCS", {"start": v(-70, -90) * mm, "end": v(70, -90) * mm, "construction": true});
            skLineSegment(sketch, "E92.MirrorCS", {"start": v(0, -120) * mm, "end": v(0, -95.69) * mm, "construction": true});
            skCircle(sketch, "E93.MirrorC", {"center": v(0, -120) * mm, "radius": 6 * mm});
            skLineSegment(sketch, "E94.MirrorCS", {"start": v(15, -120) * mm, "end": v(15, -108) * mm});
            skLineSegment(sketch, "E95.MirrorCS", {"start": v(-33, -90) * mm, "end": v(-15, -108) * mm});
            skLineSegment(sketch, "E96.MirrorCS", {"start": v(15, -108) * mm, "end": v(33, -90) * mm});
            skLineSegment(sketch, "E97.MirrorCS", {"start": v(-15, -108) * mm, "end": v(-15, -120) * mm});
            skSolve(sketch);
        }
        {
            var Q0;
            {var subQ0=sQuery(id+"F17.wireOp",EDGE,"E79");Q0=makeQuery(id+"F17.imprint","IMPRINT",FACE,{"disambiguationData":[TD([[makeQuery(id+"F17.imprint","IMPRINT",EDGE,{"derivedFrom":subQ0}),-1.0]])]});}
            var Q1;
            Q1=makeQuery(id+"F16.imprint","IMPRINT",FACE,{"disambiguationData":[TD([[makeQuery(id+"F16.imprint","IMPRINT",EDGE,{"derivedFrom":makeQuery(id+"F1.opExtrude","CAP_EDGE",EDGE,{"disambiguationData":[OSD([sQuery(id+"F0.wireOp",EDGE,"E1.bottom")])],"isStart":true})}),1.0]])]});
            var Q2;
            Q2=makeQuery(id+"F17.imprint","IMPRINT",FACE,{"disambiguationData":[TD([[makeQuery(id+"F17.imprint","IMPRINT",EDGE,{"derivedFrom":sQuery(id+"F17.wireOp",EDGE,"E89.MirrorCS")}),-1.0]])]});
            var Q3;
            Q3=makeQuery(id+"F2.opExtrude","CAP_FACE",FACE,{"disambiguationData":[OSD([sQuery(id+"F0.wireOp",EDGE,"E12"),sQuery(id+"F0.wireOp",EDGE,"E13"),sQuery(id+"F0.wireOp",EDGE,"E14"),sQuery(id+"F0.wireOp",EDGE,"E15"),sQuery(id+"F0.wireOp",EDGE,"E17.filletArc"),sQuery(id+"F0.wireOp",EDGE,"E18.filletArc"),sQuery(id+"F0.wireOp",EDGE,"E19.filletArc"),sQuery(id+"F0.wireOp",EDGE,"E20.filletArc"),sQuery(id+"F0.wireOp",EDGE,"E25.0"),sQuery(id+"F0.wireOp",EDGE,"E25.1"),sQuery(id+"F0.wireOp",EDGE,"E25.2"),sQuery(id+"F0.wireOp",EDGE,"E25.3"),sQuery(id+"F0.wireOp",EDGE,"E25.4"),sQuery(id+"F0.wireOp",EDGE,"E25.5"),sQuery(id+"F0.wireOp",EDGE,"E25.6"),sQuery(id+"F0.wireOp",EDGE,"E25.7")])],"isStart":false});
            extrude(context, id + "F18", {"entities" : qUnion([Q0, Q1, Q2]), "endBound" : BoundingType.UP_TO_SURFACE, "depth" : 25 * mm, "endBoundEntityFace" : qUnion([Q3]), "offsetDistance" : 25 * mm});
        }
    });
